# Revit family: Vehicle-Restraint_BlueGiant_HVR303
name_source: partatom
category: Specialty Equipment
units: mm (PartAtom-declared; Revit-internal decimal feet)

## family parameters
Always vertical = No
Classification Number = 23.50.70.27
Cut with Voids When Loaded = No
Enable Cutting in Views = No
Maintain Annotation Orientation = No
Part Type = Normal
Room Calculation Point = No
Round Connector Dimension = Use Diameter
Shared = No
Work Plane-Based = Yes

## types (1)
- HVR303
    Arm Finish = Metal - Blue Giant - Arm Coating
    Assembly Code = E1030300
    Capacity = 32000 lbs
    Construction Details = http://www.arcat.com
    Default Elevation = 0' - 0"
    Description = Blue Giant HVR303 StrongArm Electric Vehicle Restraint
    Expected Lifespan (Years) = 0
    Green Building-LEED = http://www.arcat.com
    Installation_Fabricaton = http://www.bluegiant.com
    Keynote = 11160
    Maintenance Schedule (Months) = 0
    Manufacturer = Blue Giant Equipment Corp.
    Manufacturer Fax = 905-457-2313
    Manufacturer Website = http://www.bluegiant.com
    Model = HVR303
    Panel Material = Metal - Blue Giant - Zinc Coated Steel
    Product Data = http://www.arcat.com
    Product Properties = http://www.arcat.com
    Sales Information = http://www.bluegiant.com
    Send Message = http://admin.arcat.com
    SpecWizard = http://www.arcat.com
    Specification = http://www.arcat.com
    Standards Conformance = ANSI MH30.3 Approved
    URL = http://www.bluegiant.com
    Unit Depth = 2' - 7 3/4"
    Unit Height = 2' - 3 7/8"
    Unit Weight = 0
    Unit Width = 1' - 4 1/2"
    Warranty Duration (Years) = 0

## geometry (parser evidence)
native form markers: Blend x4, Sweep x2
no freeform markers — native parametric forms only
